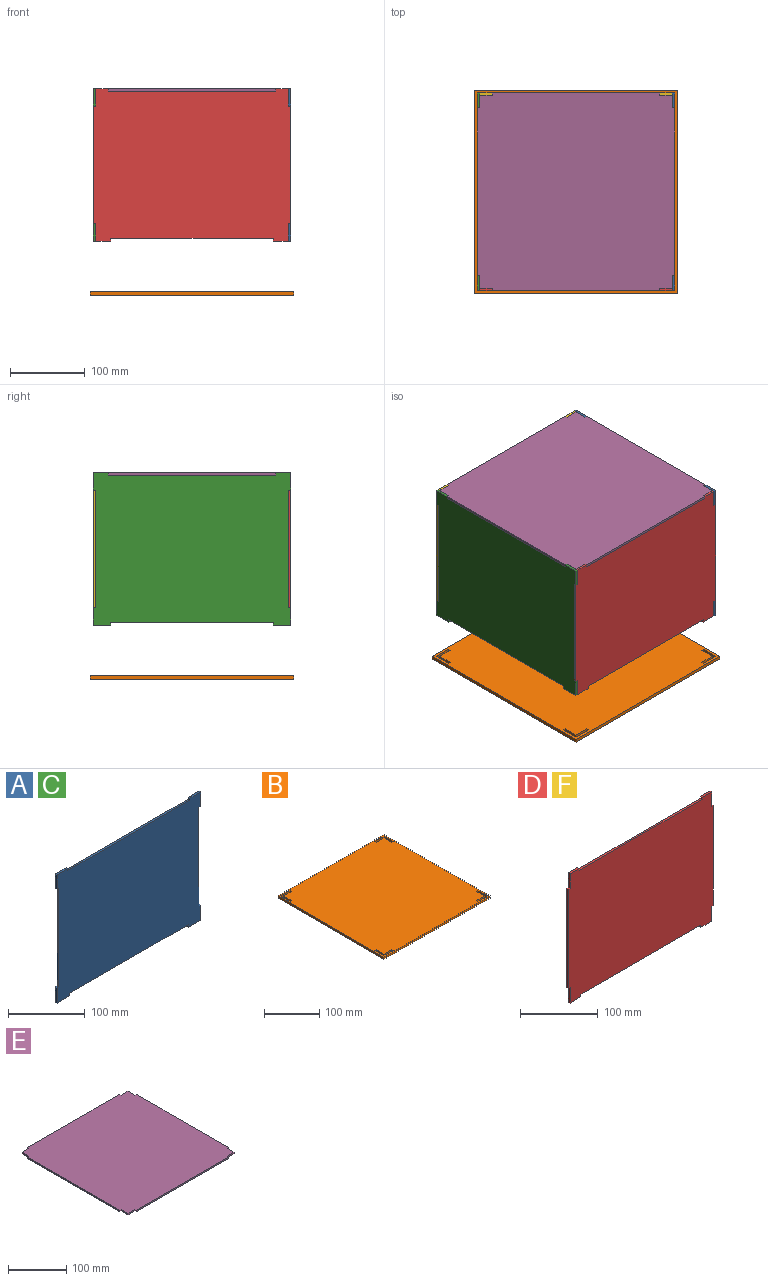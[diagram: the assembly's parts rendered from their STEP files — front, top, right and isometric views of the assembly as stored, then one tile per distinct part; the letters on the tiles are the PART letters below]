
ASSEMBLY  parts=6 mates=15
PART A: 22 faces, bbox 264x3x204 mm
  f0: plane 23x3mm, normal (-1,0,0), area 69mm2, adj f1,f19,f20,f21
  f1: plane 3x3mm, normal (0,0,-1), area 9mm2, adj f0,f2,f20,f21
  f2: plane 157x3mm, normal (-1,0,0), area 471mm2, adj f1,f3,f20,f21
  f3: plane 3x3mm, normal (0,0,1), area 9mm2, adj f2,f4,f20,f21
  f4: plane 24x3mm, normal (-1,0,0), area 72mm2, adj f3,f5,f20,f21
  f5: plane 23x3mm, normal (0,0,-1), area 69mm2, adj f4,f6,f20,f21
  f6: plane 4x3mm, normal (1,0,0), area 12mm2, adj f5,f7,f20,f21
  f7: plane 218x3mm, normal (0,0,-1), area 654mm2, adj f6,f8,f20,f21
  f8: plane 4x3mm, normal (-1,0,0), area 12mm2, adj f7,f9,f20,f21
  f9: plane 23x3mm, normal (0,0,-1), area 69mm2, adj f8,f10,f20,f21
  f10: plane 24x3mm, normal (1,0,0), area 72mm2, adj f9,f11,f20,f21
  f11: plane 3x3mm, normal (0,0,1), area 9mm2, adj f10,f12,f20,f21
  f12: plane 157x3mm, normal (1,0,0), area 471mm2, adj f11,f13,f20,f21
  f13: plane 3x3mm, normal (0,0,-1), area 9mm2, adj f12,f14,f20,f21
  f14: plane 23x3mm, normal (1,0,0), area 69mm2, adj f13,f15,f20,f21
  f15: plane 20x3mm, normal (0,0,1), area 60mm2, adj f14,f16,f20,f21
  f16: plane 3x3mm, normal (-1,0,0), area 9mm2, adj f15,f17,f20,f21
  f17: plane 224x3mm, normal (0,0,1), area 672mm2, adj f16,f18,f20,f21
  f18: plane 3x3mm, normal (1,0,0), area 9mm2, adj f17,f19,f20,f21
  f19: plane 20x3mm, normal (0,0,1), area 60mm2, adj f0,f18,f20,f21
  f20: plane 264x204mm, normal (0,-1,0), area 51370mm2, adj f0,f1,f2,f3,f4,f5,f6,f7
  f21: plane 264x204mm, normal (0,1,0), area 51370mm2, adj f0,f1,f2,f3,f4,f5,f6,f7
PART B: 30 faces, bbox 272x272x4.5 mm
  f0: plane 272x4.5mm, normal (0,-1,0), area 1224mm2, adj f1,f27,f28,f29
  f1: plane 272x4.5mm, normal (1,0,0), area 1224mm2, adj f0,f2,f28,f29
  f2: plane 272x4.5mm, normal (0,1,0), area 1224mm2, adj f1,f27,f28,f29
  f3: plane 20x4.5mm, normal (0,1,0), area 90mm2, adj f4,f23,f28,f29
  f4: plane 4.5x3.2mm, normal (1,0,0), area 14.4mm2, adj f3,f5,f28,f29
  f5: plane 23.2x4.5mm, normal (0,-1,0), area 104.4mm2, adj f4,f6,f28,f29
  f6: plane 23.2x4.5mm, normal (-1,0,0), area 104.4mm2, adj f5,f7,f28,f29
  f7: plane 4.5x3.2mm, normal (0,1,0), area 14.4mm2, adj f6,f23,f28,f29
  f8: plane 20x4.5mm, normal (1,0,0), area 90mm2, adj f9,f24,f28,f29
  f9: plane 4.5x3.2mm, normal (0,-1,0), area 14.4mm2, adj f8,f10,f28,f29
  f10: plane 23.2x4.5mm, normal (-1,0,0), area 104.4mm2, adj f9,f11,f28,f29
  f11: plane 23.2x4.5mm, normal (0,1,0), area 104.4mm2, adj f10,f12,f28,f29
  f12: plane 4.5x3.2mm, normal (1,0,0), area 14.4mm2, adj f11,f24,f28,f29
  f13: plane 20x4.5mm, normal (0,-1,0), area 90mm2, adj f14,f25,f28,f29
  f14: plane 4.5x3.2mm, normal (-1,0,0), area 14.4mm2, adj f13,f15,f28,f29
  f15: plane 23.2x4.5mm, normal (0,1,0), area 104.4mm2, adj f14,f16,f28,f29
  f16: plane 23.2x4.5mm, normal (1,0,0), area 104.4mm2, adj f15,f17,f28,f29
  f17: plane 4.5x3.2mm, normal (0,-1,0), area 14.4mm2, adj f16,f25,f28,f29
  f18: plane 20x4.5mm, normal (-1,0,0), area 90mm2, adj f19,f26,f28,f29
  f19: plane 4.5x3.2mm, normal (0,1,0), area 14.4mm2, adj f18,f20,f28,f29
  f20: plane 23.2x4.5mm, normal (1,0,0), area 104.4mm2, adj f19,f21,f28,f29
  f21: plane 23.2x4.5mm, normal (0,-1,0), area 104.4mm2, adj f20,f22,f28,f29
  f22: plane 4.5x3.2mm, normal (-1,0,0), area 14.4mm2, adj f21,f26,f28,f29
  f23: plane 20x4.5mm, normal (1,0,0), area 90mm2, adj f3,f7,f28,f29
  f24: plane 20x4.5mm, normal (0,-1,0), area 90mm2, adj f8,f12,f28,f29
  f25: plane 20x4.5mm, normal (-1,0,0), area 90mm2, adj f13,f17,f28,f29
  f26: plane 20x4.5mm, normal (0,1,0), area 90mm2, adj f18,f22,f28,f29
  f27: plane 272x4.5mm, normal (-1,0,0), area 1224mm2, adj f0,f2,f28,f29
  f28: plane 272x272mm, normal (0,0,1), area 73431mm2, adj f0,f1,f2,f3,f4,f5,f6,f7
  f29: plane 272x272mm, normal (0,0,-1), area 73431mm2, adj f0,f1,f2,f3,f4,f5,f6,f7
PART C: same geometry as A
PART D: 22 faces, bbox 264x3x204 mm
  f0: plane 20x3mm, normal (0,0,-1), area 60mm2, adj f1,f19,f20,f21
  f1: plane 4x3mm, normal (1,0,0), area 12mm2, adj f0,f2,f20,f21
  f2: plane 218x3mm, normal (0,0,-1), area 654mm2, adj f1,f3,f20,f21
  f3: plane 4x3mm, normal (-1,0,0), area 12mm2, adj f2,f4,f20,f21
  f4: plane 20x3mm, normal (0,0,-1), area 60mm2, adj f3,f5,f20,f21
  f5: plane 24x3mm, normal (1,0,0), area 72mm2, adj f4,f6,f20,f21
  f6: plane 3x3mm, normal (0,0,-1), area 9mm2, adj f5,f7,f20,f21
  f7: plane 157x3mm, normal (1,0,0), area 471mm2, adj f6,f8,f20,f21
  f8: plane 3x3mm, normal (0,0,1), area 9mm2, adj f7,f9,f20,f21
  f9: plane 23x3mm, normal (1,0,0), area 69mm2, adj f8,f10,f20,f21
  f10: plane 17x3mm, normal (0,0,1), area 51mm2, adj f9,f11,f20,f21
  f11: plane 3x3mm, normal (-1,0,0), area 9mm2, adj f10,f12,f20,f21
  f12: plane 224x3mm, normal (0,0,1), area 672mm2, adj f11,f13,f20,f21
  f13: plane 3x3mm, normal (1,0,0), area 9mm2, adj f12,f14,f20,f21
  f14: plane 17x3mm, normal (0,0,1), area 51mm2, adj f13,f15,f20,f21
  f15: plane 23x3mm, normal (-1,0,0), area 69mm2, adj f14,f16,f20,f21
  f16: plane 3x3mm, normal (0,0,1), area 9mm2, adj f15,f17,f20,f21
  f17: plane 157x3mm, normal (-1,0,0), area 471mm2, adj f16,f18,f20,f21
  f18: plane 3x3mm, normal (0,0,-1), area 9mm2, adj f17,f19,f20,f21
  f19: plane 24x3mm, normal (-1,0,0), area 72mm2, adj f0,f18,f20,f21
  f20: plane 264x204mm, normal (0,-1,0), area 52030mm2, adj f0,f1,f2,f3,f4,f5,f6,f7
  f21: plane 264x204mm, normal (0,1,0), area 52030mm2, adj f0,f1,f2,f3,f4,f5,f6,f7
PART E: 22 faces, bbox 264x264x3 mm
  f0: plane 3x3mm, normal (-1,0,0), area 9mm2, adj f1,f19,f20,f21
  f1: plane 224x3mm, normal (0,-1,0), area 672mm2, adj f0,f2,f20,f21
  f2: plane 3x3mm, normal (1,0,0), area 9mm2, adj f1,f3,f20,f21
  f3: plane 17x3mm, normal (0,-1,0), area 51mm2, adj f2,f4,f20,f21
  f4: plane 17x3mm, normal (1,0,0), area 51mm2, adj f3,f5,f20,f21
  f5: plane 3x3mm, normal (0,-1,0), area 9mm2, adj f4,f6,f20,f21
  f6: plane 224x3mm, normal (1,0,0), area 672mm2, adj f5,f7,f20,f21
  f7: plane 3x3mm, normal (0,1,0), area 9mm2, adj f6,f8,f20,f21
  f8: plane 17x3mm, normal (1,0,0), area 51mm2, adj f7,f9,f20,f21
  f9: plane 17x3mm, normal (0,1,0), area 51mm2, adj f8,f10,f20,f21
  f10: plane 3x3mm, normal (1,0,0), area 9mm2, adj f9,f11,f20,f21
  f11: plane 224x3mm, normal (0,1,0), area 672mm2, adj f10,f12,f20,f21
  f12: plane 3x3mm, normal (-1,0,0), area 9mm2, adj f11,f13,f20,f21
  f13: plane 17x3mm, normal (0,1,0), area 51mm2, adj f12,f14,f20,f21
  f14: plane 17x3mm, normal (-1,0,0), area 51mm2, adj f13,f15,f20,f21
  f15: plane 3x3mm, normal (0,1,0), area 9mm2, adj f14,f16,f20,f21
  f16: plane 224x3mm, normal (-1,0,0), area 672mm2, adj f15,f17,f20,f21
  f17: plane 3x3mm, normal (0,-1,0), area 9mm2, adj f16,f18,f20,f21
  f18: plane 17x3mm, normal (-1,0,0), area 51mm2, adj f17,f19,f20,f21
  f19: plane 17x3mm, normal (0,-1,0), area 51mm2, adj f0,f18,f20,f21
  f20: plane 264x264mm, normal (0,0,1), area 69252mm2, adj f0,f1,f2,f3,f4,f5,f6,f7
  f21: plane 264x264mm, normal (0,0,-1), area 69252mm2, adj f0,f1,f2,f3,f4,f5,f6,f7
PART F: same geometry as D
PLACE A rot(axis=(0,0,-1),90deg) t=(-98.92,37.69,-1.58)mm
PLACE B rot(axis=(0,-1,0),180deg) t=(-230.92,377.09,-58.29)mm
PLACE C rot(axis=(0,0,1),90deg) t=(-362.92,716.49,-1.58)mm
PLACE D t=(-201.32,248.09,3.91)mm
PLACE E t=(-187.39,85.79,205.82)mm
PLACE F t=(-201.32,509.09,3.91)mm
MATE planar D.f15 <-> C.f20  axis (-1,0,0) through (-359.92,246.59,201.82)mm
MATE planar E.f11 <-> F.f21  axis (0,1,0) through (-230.92,509.09,211.82)mm
MATE planar F.f12 <-> E.f21  axis (0,0,1) through (-230.92,507.59,210.32)mm
MATE planar E.f20 <-> D.f14  axis (0,0,1) through (-230.92,377.09,213.32)mm
MATE planar D.f20 <-> A.f14  axis (0,-1,0) through (-118.92,245.09,210.32)mm
MATE planar A.f20 <-> D.f9  axis (-1,0,0) through (-101.92,377.09,111.69)mm
MATE planar E.f16 <-> C.f21  axis (-1,0,0) through (-362.92,377.09,211.82)mm
MATE planar F.f20 <-> B.f26  axis (0,-1,0) through (-230.92,506.09,111.71)mm
MATE planar F.f20 <-> C.f12  axis (0,-1,0) through (-230.92,506.09,111.71)mm
MATE planar C.f20 <-> B.f8  axis (1,0,0) through (-359.92,377.09,111.69)mm
MATE planar D.f20 <-> C.f0  axis (0,-1,0) through (-230.92,245.09,111.71)mm
MATE planar F.f5 <-> B.f18  axis (1,0,0) through (-101.92,507.59,21.32)mm
MATE planar B.f25 <-> A.f20  axis (1,0,0) through (-101.92,258.09,-60.54)mm
MATE planar E.f21 <-> C.f17  axis (0,0,-1) through (-230.92,377.09,210.32)mm
MATE planar E.f20 <-> A.f19  axis (0,0,1) through (-230.92,377.09,213.32)mm
